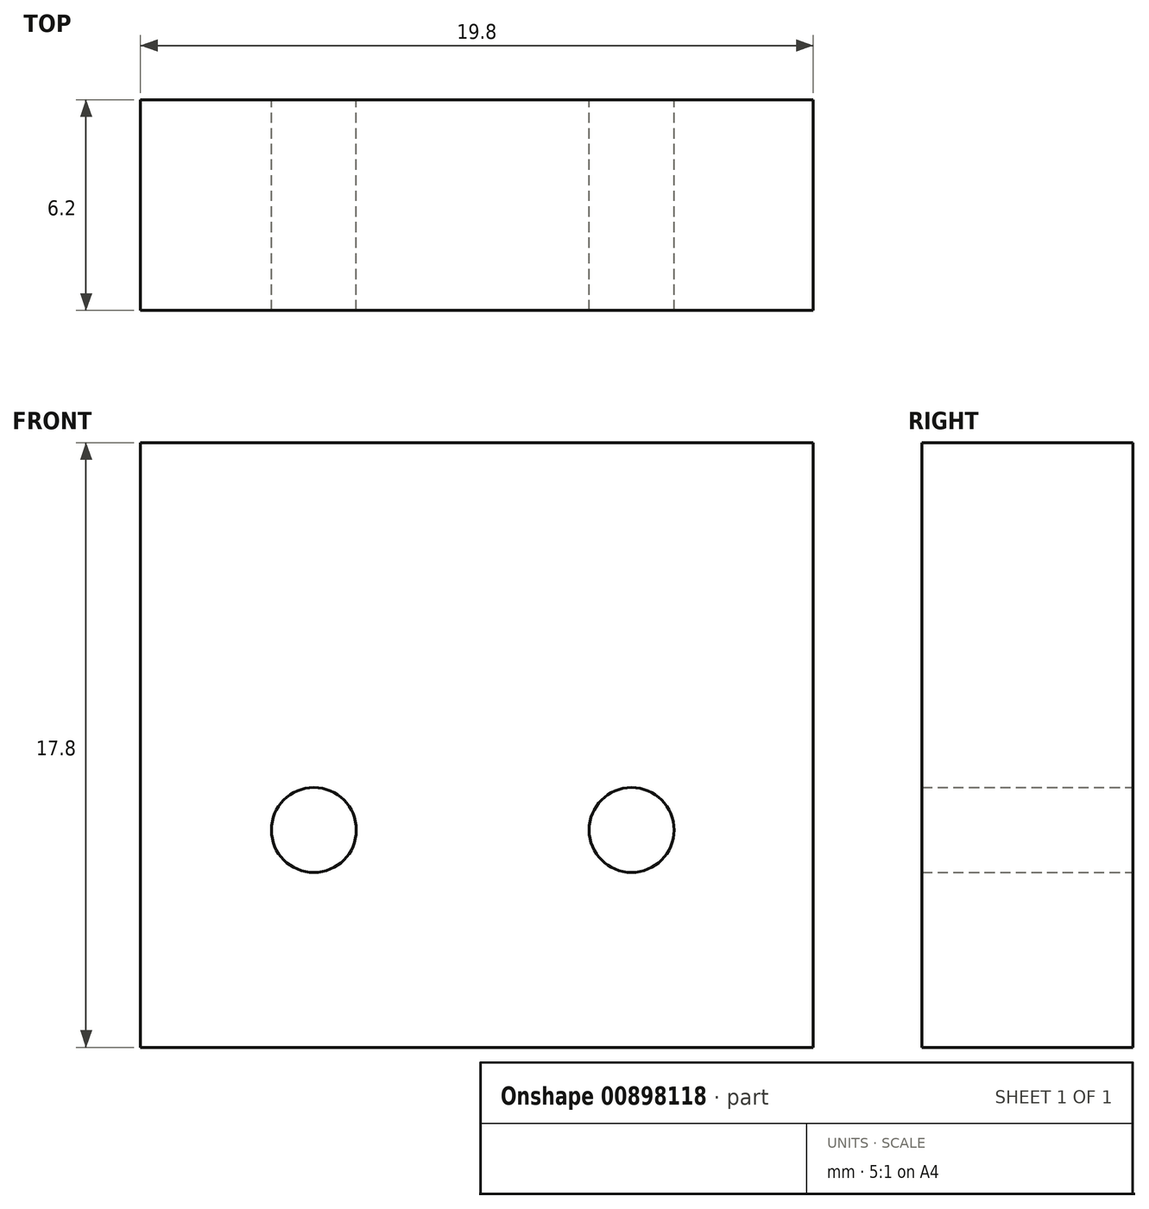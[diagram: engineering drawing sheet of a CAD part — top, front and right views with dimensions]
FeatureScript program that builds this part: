
annotation { "Feature Type Name" : "Feature", "Feature Type Description" : "" }
export const myFeature = defineFeature(function(context is Context, id is Id, definition is map)
    precondition{}
    {
        {
            var Q0;
            Q0=qCreatedBy(makeId("Front.planeOp"),FACE);
            var sketch = newSketch(context, id + "F0", { "sketchPlane" : qUnion([Q0])});
            skLineSegment(sketch, "E0.bottom", {"start": v(-9.9, 17.8) * mm, "end": v(9.9, 17.8) * mm});
            skLineSegment(sketch, "E0.top", {"start": v(-9.9, 0) * mm, "end": v(9.9, 0) * mm});
            skLineSegment(sketch, "E0.left", {"start": v(-9.9, 17.8) * mm, "end": v(-9.9, 0) * mm});
            skLineSegment(sketch, "E0.right", {"start": v(9.9, 17.8) * mm, "end": v(9.9, 0) * mm});
            skPoint(sketch, "E1", {"position": v(-9.9, 3.5) * mm});
            skPoint(sketch, "E2", {"position": v(-9.9, 6.4) * mm});
            skPoint(sketch, "E3", {"position": v(-4.8, 6.4) * mm});
            skPoint(sketch, "E4", {"position": v(4.55, 6.4) * mm});
            skCircle(sketch, "E5", {"center": v(-4.8, 6.4) * mm, "radius": 1.25 * mm});
            skCircle(sketch, "E6", {"center": v(4.55, 6.4) * mm, "radius": 1.25 * mm});
            skSolve(sketch);
        }
        {
            var Q0;
            Q0=makeQuery(id+"F0.imprint","IMPRINT",FACE,{"disambiguationData":[TD([[makeQuery(id+"F0.imprint","IMPRINT",EDGE,{"derivedFrom":sQuery(id+"F0.wireOp",EDGE,"E0.bottom")}),-1.0]])]});
            extrude(context, id + "F1", {"entities" : qUnion([Q0]), "depth" : 6.2 * mm, "offsetDistance" : 25 * mm});
        }
    });
